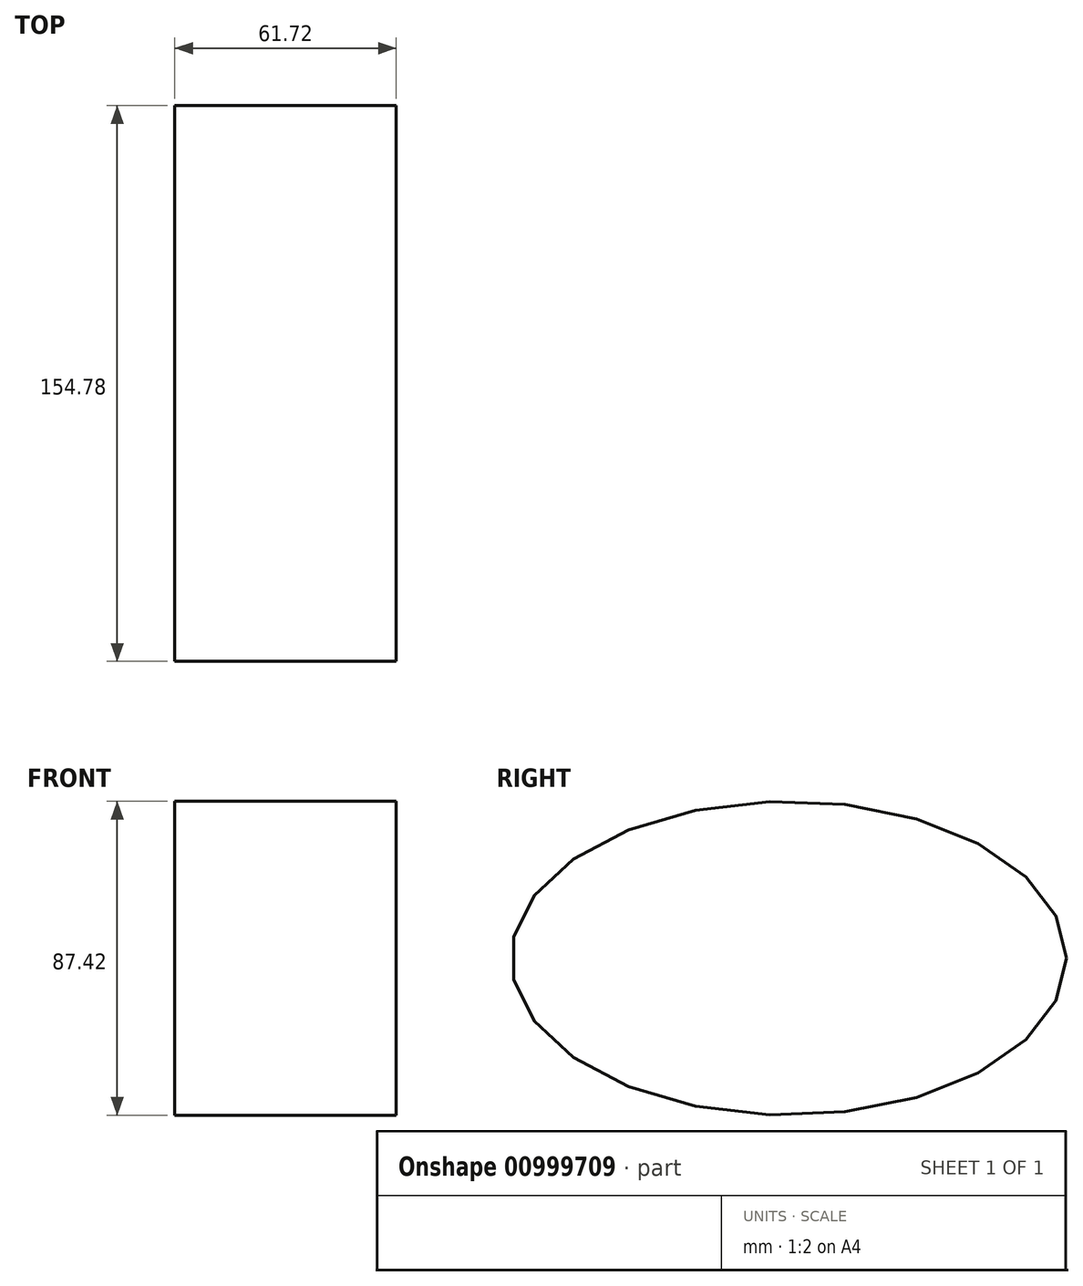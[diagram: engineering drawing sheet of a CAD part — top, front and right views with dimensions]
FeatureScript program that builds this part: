
annotation { "Feature Type Name" : "Feature", "Feature Type Description" : "" }
export const myFeature = defineFeature(function(context is Context, id is Id, definition is map)
    precondition{}
    {
        {
            var Q0;
            Q0=qCreatedBy(makeId("Right.planeOp"),FACE);
            var sketch = newSketch(context, id + "F0", { "sketchPlane" : qUnion([Q0])});
            skEllipse(sketch, "E0", {"center": v(0, 0) * mm, "majorRadius": 77.39 * mm, "minorRadius": 43.7 * mm, "majorAxis": v(1, 0)});
            skSolve(sketch);
        }
        {
            var Q0;
            Q0=makeQuery(id+"F0.imprint","IMPRINT",FACE,{"disambiguationData":[TD([[makeQuery(id+"F0.imprint","IMPRINT",EDGE,{"derivedFrom":sQuery(id+"F0.wireOp",EDGE,"E0")}),1.0]])]});
            extrude(context, id + "F1", {"entities" : qUnion([Q0]), "depth" : 61.72 * mm, "offsetDistance" : 25.4 * mm});
        }
    });
